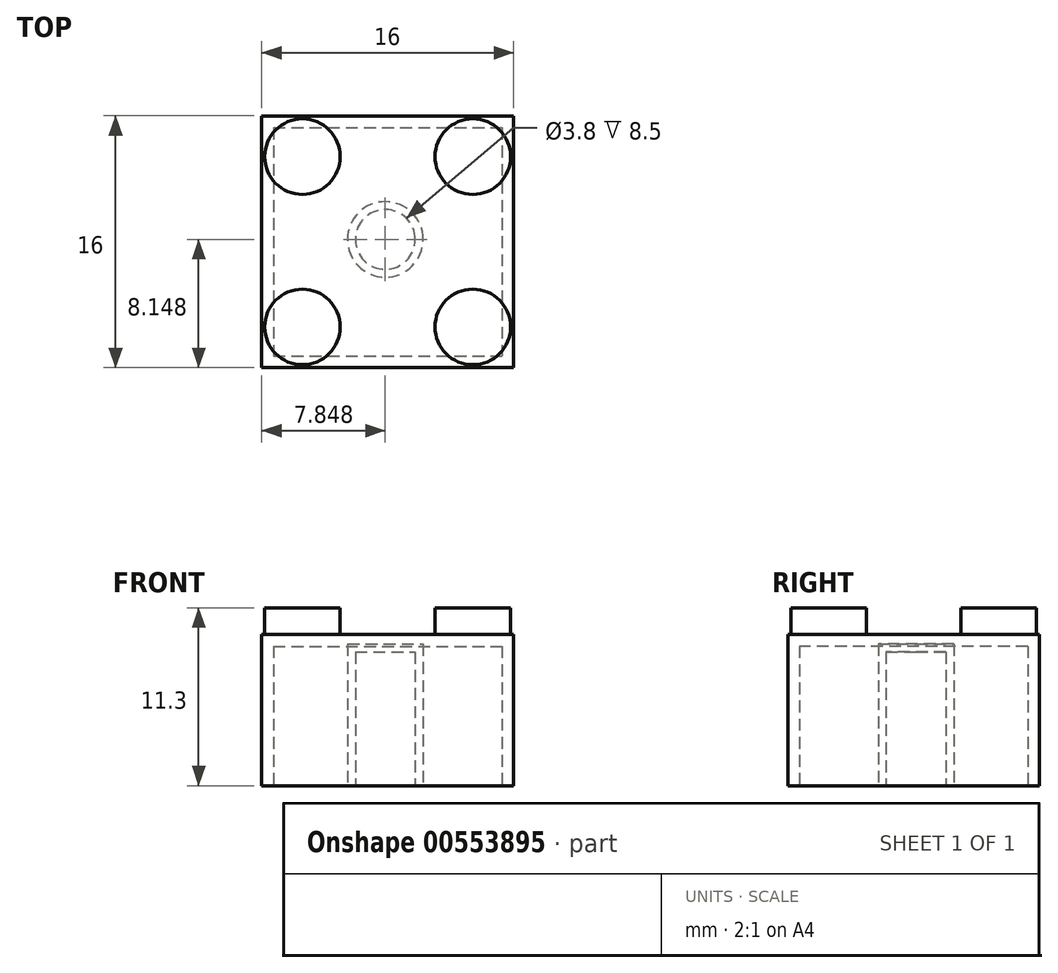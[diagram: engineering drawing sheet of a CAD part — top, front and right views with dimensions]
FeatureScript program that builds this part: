
annotation { "Feature Type Name" : "Feature", "Feature Type Description" : "" }
export const myFeature = defineFeature(function(context is Context, id is Id, definition is map)
    precondition{}
    {
        {
            var Q0;
            Q0=qCreatedBy(makeId("Top.planeOp"),FACE);
            var sketch = newSketch(context, id + "F0", { "sketchPlane" : qUnion([Q0])});
            skLineSegment(sketch, "E0.bottom", {"start": v(-58.94, 32.32) * mm, "end": v(-42.94, 32.32) * mm});
            skLineSegment(sketch, "E0.top", {"start": v(-58.94, 16.32) * mm, "end": v(-42.94, 16.32) * mm});
            skLineSegment(sketch, "E0.left", {"start": v(-58.94, 32.32) * mm, "end": v(-58.94, 16.32) * mm});
            skLineSegment(sketch, "E0.right", {"start": v(-42.94, 32.32) * mm, "end": v(-42.94, 16.32) * mm});
            skSolve(sketch);
        }
        {
            var Q0;
            Q0 = qSketchRegion(id + "F0", true);
            extrude(context, id + "F1", {"entities" : qUnion([Q0]), "depth" : 9.6 * mm, "offsetDistance" : 25 * mm});
        }
        {
            var Q0;
            Q0=makeQuery(id+"F1.opExtrude","CAP_FACE",FACE,{"disambiguationData":[OSD([sQuery(id+"F0.wireOp",EDGE,"E0.bottom"),sQuery(id+"F0.wireOp",EDGE,"E0.top"),sQuery(id+"F0.wireOp",EDGE,"E0.left"),sQuery(id+"F0.wireOp",EDGE,"E0.right")])],"isStart":true});
            var sketch = newSketch(context, id + "F2", { "sketchPlane" : qUnion([Q0])});
            skSolve(sketch);
        }
        {
            var Q0;
            Q0=makeQuery(id+"F1.opExtrude","CAP_FACE",FACE,{"disambiguationData":[OSD([sQuery(id+"F0.wireOp",EDGE,"E0.bottom"),sQuery(id+"F0.wireOp",EDGE,"E0.top"),sQuery(id+"F0.wireOp",EDGE,"E0.left"),sQuery(id+"F0.wireOp",EDGE,"E0.right")])],"isStart":true});
            shell(context, id + "F3", {"entities" : qUnion([Q0]), "thickness" : 0.75 * mm});
        }
        {
            var Q0;
            Q0=makeQuery(id+"F1.opExtrude","CAP_FACE",FACE,{"disambiguationData":[OSD([sQuery(id+"F0.wireOp",EDGE,"E0.bottom"),sQuery(id+"F0.wireOp",EDGE,"E0.top"),sQuery(id+"F0.wireOp",EDGE,"E0.left"),sQuery(id+"F0.wireOp",EDGE,"E0.right")])],"isStart":false});
            var sketch = newSketch(context, id + "F4", { "sketchPlane" : qUnion([Q0])});
            skSolve(sketch);
        }
        {
            var Q0;
            Q0=makeQuery(id+"F2.imprint","IMPRINT",FACE,{"disambiguationData":[TD([[makeQuery(id+"F2.imprint","IMPRINT",EDGE,{"derivedFrom":makeQuery(id+"F1.opExtrude","CAP_EDGE",EDGE,{"disambiguationData":[OSD([sQuery(id+"F0.wireOp",EDGE,"E0.bottom")])],"isStart":true})}),1.0]])]});
            var sketch = newSketch(context, id + "F5", { "sketchPlane" : qUnion([Q0])});
            skCircle(sketch, "E1", {"center": v(-51.1, -24.47) * mm, "radius": 2.4 * mm});
            skSolve(sketch);
        }
        {
            var Q0;
            Q0 = qSketchRegion(id + "F5", true);
            extrude(context, id + "F6", {"entities" : qUnion([Q0]), "oppositeDirection" : true, "depth" : 9 * mm, "offsetDistance" : 25 * mm});
        }
        {
            var Q0;
            Q0=makeQuery(id+"F6.opExtrude","CAP_FACE",FACE,{"disambiguationData":[OSD([sQuery(id+"F5.wireOp",EDGE,"E1")])],"isStart":true});
            shell(context, id + "F7", {"entities" : qUnion([Q0]), "thickness" : 0.5 * mm});
        }
        {
            var Q0;
            Q0=makeQuery(id+"F4.imprint","IMPRINT",FACE,{"disambiguationData":[TD([[makeQuery(id+"F4.imprint","IMPRINT",EDGE,{"derivedFrom":makeQuery(id+"F1.opExtrude","CAP_EDGE",EDGE,{"disambiguationData":[OSD([sQuery(id+"F0.wireOp",EDGE,"E0.bottom")])],"isStart":false})}),-1.0]])]});
            var sketch = newSketch(context, id + "F8", { "sketchPlane" : qUnion([Q0])});
            skCircle(sketch, "E2", {"center": v(-56.35, 29.73) * mm, "radius": 2.4 * mm});
            skSolve(sketch);
        }
        {
            var Q0;
            Q0 = qSketchRegion(id + "F8", true);
            extrude(context, id + "F9", {"entities" : qUnion([Q0]), "operationType" : NewBodyOperationType.ADD, "depth" : 1.7 * mm, "offsetDistance" : 25 * mm});
        }
        {
            var Q0;
            Q0=makeQuery(id+"F4.imprint","IMPRINT",FACE,{"disambiguationData":[TD([[makeQuery(id+"F4.imprint","IMPRINT",EDGE,{"derivedFrom":makeQuery(id+"F1.opExtrude","CAP_EDGE",EDGE,{"disambiguationData":[OSD([sQuery(id+"F0.wireOp",EDGE,"E0.bottom")])],"isStart":false})}),-1.0]])]});
            var sketch = newSketch(context, id + "F10", { "sketchPlane" : qUnion([Q0])});
            skCircle(sketch, "E3", {"center": v(-45.53, 29.73) * mm, "radius": 2.4 * mm});
            skSolve(sketch);
        }
        {
            var Q0;
            Q0 = qSketchRegion(id + "F10", true);
            extrude(context, id + "F11", {"entities" : qUnion([Q0]), "operationType" : NewBodyOperationType.ADD, "depth" : 1.7 * mm, "offsetDistance" : 25 * mm});
        }
        {
            var Q0;
            Q0=makeQuery(id+"F4.imprint","IMPRINT",FACE,{"disambiguationData":[TD([[makeQuery(id+"F4.imprint","IMPRINT",EDGE,{"derivedFrom":makeQuery(id+"F1.opExtrude","CAP_EDGE",EDGE,{"disambiguationData":[OSD([sQuery(id+"F0.wireOp",EDGE,"E0.bottom")])],"isStart":false})}),-1.0]])]});
            var sketch = newSketch(context, id + "F12", { "sketchPlane" : qUnion([Q0])});
            skCircle(sketch, "E4", {"center": v(-56.35, 18.9) * mm, "radius": 2.4 * mm});
            skSolve(sketch);
        }
        {
            var Q0;
            Q0 = qSketchRegion(id + "F12", true);
            extrude(context, id + "F13", {"entities" : qUnion([Q0]), "operationType" : NewBodyOperationType.ADD, "depth" : 1.7 * mm, "offsetDistance" : 25 * mm});
        }
        {
            var Q0;
            Q0=makeQuery(id+"F4.imprint","IMPRINT",FACE,{"disambiguationData":[TD([[makeQuery(id+"F4.imprint","IMPRINT",EDGE,{"derivedFrom":makeQuery(id+"F1.opExtrude","CAP_EDGE",EDGE,{"disambiguationData":[OSD([sQuery(id+"F0.wireOp",EDGE,"E0.bottom")])],"isStart":false})}),-1.0]])]});
            var sketch = newSketch(context, id + "F14", { "sketchPlane" : qUnion([Q0])});
            skCircle(sketch, "E5", {"center": v(-45.53, 18.9) * mm, "radius": 2.4 * mm});
            skSolve(sketch);
        }
        {
            var Q0;
            Q0 = qSketchRegion(id + "F14", true);
            extrude(context, id + "F15", {"entities" : qUnion([Q0]), "operationType" : NewBodyOperationType.ADD, "depth" : 1.7 * mm, "offsetDistance" : 25 * mm});
        }
    });
